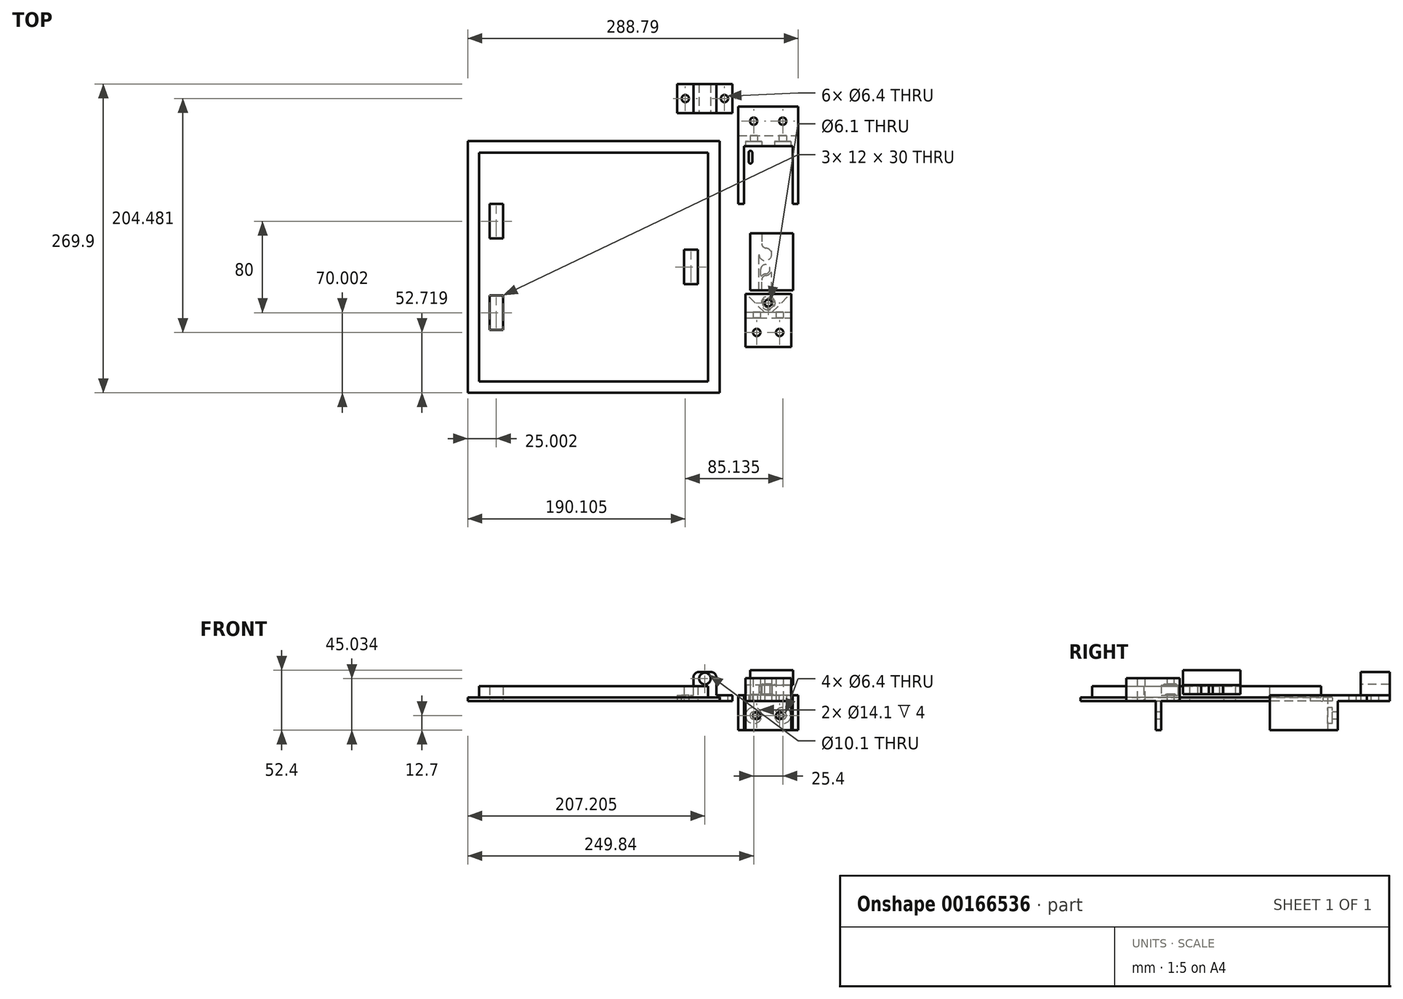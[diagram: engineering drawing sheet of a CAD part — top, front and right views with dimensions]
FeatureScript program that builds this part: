
annotation { "Feature Type Name" : "Feature", "Feature Type Description" : "" }
export const myFeature = defineFeature(function(context is Context, id is Id, definition is map)
    precondition{}
    {
        {
            var Q0;
            Q0=qCreatedBy(makeId("Top.planeOp"),FACE);
            var sketch = newSketch(context, id + "F0", { "sketchPlane" : qUnion([Q0])});
            skPoint(sketch, "E0.5", {"position": v(15.5, -15.5) * mm});
            skPoint(sketch, "E0.6", {"position": v(-15.5, -15.5) * mm});
            skPoint(sketch, "E0.7", {"position": v(-15.5, 15.5) * mm});
            skPoint(sketch, "E0.8", {"position": v(15.5, 15.5) * mm});
            skLineSegment(sketch, "E1.0", {"start": v(-21.25, 21.25) * mm, "end": v(-21.25, -21.25) * mm});
            skLineSegment(sketch, "E1.1", {"start": v(21.25, 21.25) * mm, "end": v(-21.25, 21.25) * mm});
            skLineSegment(sketch, "E1.2", {"start": v(21.25, 21.25) * mm, "end": v(21.25, -21.25) * mm});
            skLineSegment(sketch, "E1.3", {"start": v(21.25, -21.25) * mm, "end": v(-21.25, -21.25) * mm});
            skCircle(sketch, "E2.0", {"center": v(0, 0) * mm, "radius": 11.25 * mm});
            skCircle(sketch, "E3", {"center": v(-15.5, 15.5) * mm, "radius": 1.52 * mm});
            skCircle(sketch, "E4", {"center": v(15.5, 15.5) * mm, "radius": 1.52 * mm});
            skCircle(sketch, "E5", {"center": v(15.5, -15.5) * mm, "radius": 1.52 * mm});
            skCircle(sketch, "E6", {"center": v(-15.5, -15.5) * mm, "radius": 1.52 * mm});
            skLineSegment(sketch, "E7", {"start": v(-21.25, 21.25) * mm, "end": v(21.25, -21.25) * mm, "construction": true});
            skSolve(sketch);
        }
        {
            var Q0;
            Q0=qCreatedBy(makeId("Front.planeOp"),FACE);
            cPlane(context, id + "F1", {"entities" : qUnion([Q0]), "cplaneType" : CPlaneType.OFFSET, "offset" : 50 * mm, "oppositeDirection" : true, "width" : 150 * mm, "height" : 150 * mm});
        }
        {
            var Q0;
            Q0=qCreatedBy(id+"F1.planeOp",FACE);
            var sketch = newSketch(context, id + "F2", { "sketchPlane" : qUnion([Q0])});
            skLineSegment(sketch, "E8.bottom", {"start": v(-79.49, 5) * mm, "end": v(-65.39, 5) * mm});
            skLineSegment(sketch, "E8.top", {"start": v(-79.49, 0) * mm, "end": v(-31.19, 0) * mm});
            skLineSegment(sketch, "E8.left", {"start": v(-79.49, 5) * mm, "end": v(-79.49, 0) * mm});
            skLineSegment(sketch, "E8.right", {"start": v(-31.19, 5) * mm, "end": v(-31.19, 0) * mm});
            skCircle(sketch, "E9", {"center": v(-55.34, 19.63) * mm, "radius": 5.05 * mm});
            skLineSegment(sketch, "E10.bottom", {"start": v(-2.5, 24) * mm, "end": v(2.5, 24) * mm, "construction": true});
            skLineSegment(sketch, "E10.top", {"start": v(-2.5, 0) * mm, "end": v(2.5, 0) * mm, "construction": true});
            skLineSegment(sketch, "E10.left", {"start": v(-2.5, 24) * mm, "end": v(-2.5, 0) * mm, "construction": true});
            skLineSegment(sketch, "E10.right", {"start": v(2.5, 24) * mm, "end": v(2.5, 0) * mm, "construction": true});
            skLineSegment(sketch, "E11", {"start": v(-61.34, 27) * mm, "end": v(-49.34, 27) * mm, "construction": true});
            skCircle(sketch, "E12", {"center": v(-55.34, 19.63) * mm, "radius": 9.5 * mm, "construction": true});
            skPoint(sketch, "E13", {"position": v(-55.34, 5) * mm});
            skArc(sketch, "E14", {"start": v(-65.24, 21.36) * mm, "mid": v(-55.34, 9.58) * mm, "end": v(-45.43, 21.36) * mm});
            skLineSegment(sketch, "E15", {"start": v(-65.39, 5) * mm, "end": v(-65.39, 19.63) * mm});
            skLineSegment(sketch, "E16", {"start": v(-45.29, 5) * mm, "end": v(-45.29, 19.63) * mm});
            skLineSegment(sketch, "E17", {"start": v(-65.39, 5) * mm, "end": v(-45.29, 5) * mm});
            skLineSegment(sketch, "E18", {"start": v(-45.29, 5) * mm, "end": v(-31.19, 5) * mm});
            skLineSegment(sketch, "E19", {"start": v(-72.44, 6.24) * mm, "end": v(-72.44, -2.4) * mm, "construction": true});
            skPoint(sketch, "E19.startSnap0", {"position": v(-72.44, 5) * mm});
            skLineSegment(sketch, "E20", {"start": v(-38.24, 7.18) * mm, "end": v(-38.24, -1.8) * mm, "construction": true});
            skPoint(sketch, "E20.startSnap0", {"position": v(-38.24, 5) * mm});
            skPoint(sketch, "E21", {"position": v(0, 0) * mm});
            skLineSegment(sketch, "E22", {"start": v(-60.31, 25.5) * mm, "end": v(-50.36, 25.5) * mm});
            skPoint(sketch, "E23.visualSharp", {"position": v(-63.5, 25.5) * mm});
            skArc(sketch, "E23.filletArc", {"start": v(-60.31, 25.5) * mm, "mid": v(-63.53, 24.33) * mm, "end": v(-65.24, 21.36) * mm});
            skPoint(sketch, "E24.visualSharp", {"position": v(-47.17, 25.5) * mm});
            skArc(sketch, "E24.filletArc", {"start": v(-45.43, 21.36) * mm, "mid": v(-47.14, 24.33) * mm, "end": v(-50.36, 25.5) * mm});
            skLineSegment(sketch, "E25", {"start": v(-12.3, 2.5) * mm, "end": v(8.31, 2.5) * mm, "construction": true});
            skLineSegment(sketch, "E26.bottom", {"start": v(7, 5) * mm, "end": v(-7, 5) * mm, "construction": true});
            skLineSegment(sketch, "E26.top", {"start": v(7, 6) * mm, "end": v(-7, 6) * mm, "construction": true});
            skLineSegment(sketch, "E26.left", {"start": v(7, 5) * mm, "end": v(7, 6) * mm, "construction": true});
            skLineSegment(sketch, "E26.right", {"start": v(-7, 5) * mm, "end": v(-7, 6) * mm, "construction": true});
            skPoint(sketch, "E26.middle", {"position": v(0, 5.5) * mm});
            skPoint(sketch, "E26.middle.positionSnap0", {"position": v(0, 24) * mm});
            skPoint(sketch, "E26.centerSnap0", {"position": v(0, 24) * mm});
            skLineSegment(sketch, "E27.bottom", {"start": v(6.1, 6) * mm, "end": v(-6.1, 6) * mm, "construction": true});
            skLineSegment(sketch, "E27.top", {"start": v(6.1, 14) * mm, "end": v(-6.1, 14) * mm, "construction": true});
            skLineSegment(sketch, "E27.left", {"start": v(6.1, 6) * mm, "end": v(6.1, 14) * mm, "construction": true});
            skLineSegment(sketch, "E27.right", {"start": v(-6.1, 6) * mm, "end": v(-6.1, 14) * mm, "construction": true});
            skPoint(sketch, "E27.middle", {"position": v(0, 10) * mm});
            skLineSegment(sketch, "E28.bottom", {"start": v(-7, 14) * mm, "end": v(7, 14) * mm, "construction": true});
            skLineSegment(sketch, "E28.top", {"start": v(-7, 21.5) * mm, "end": v(7, 21.5) * mm, "construction": true});
            skLineSegment(sketch, "E28.left", {"start": v(-7, 14) * mm, "end": v(-7, 21.5) * mm, "construction": true});
            skLineSegment(sketch, "E28.right", {"start": v(7, 14) * mm, "end": v(7, 21.5) * mm, "construction": true});
            skPoint(sketch, "E28.middle", {"position": v(0, 17.75) * mm});
            skSolve(sketch);
        }
        {
            var Q0;
            Q0=makeQuery(id+"F2.imprint","IMPRINT",FACE,{"disambiguationData":[TD([[makeQuery(id+"F2.imprint","IMPRINT",EDGE,{"derivedFrom":sQuery(id+"F2.wireOp",EDGE,"E8.bottom")}),-1.0]])]});
            var Q1;
            {var subQ0=sQuery(id+"F2.wireOp",EDGE,"E15");Q1=makeQuery(id+"F2.imprint","IMPRINT",FACE,{"disambiguationData":[TD([[makeQuery(id+"F2.imprint","IMPRINT",EDGE,{"derivedFrom":subQ0}),-1.0]])]});}
            var Q2;
            Q2=makeQuery(id+"F2.imprint","IMPRINT",FACE,{"disambiguationData":[TD([[makeQuery(id+"F2.imprint","IMPRINT",EDGE,{"derivedFrom":sQuery(id+"F2.wireOp",EDGE,"E9")}),-1.0]])]});
            extrude(context, id + "F3", {"entities" : qUnion([Q0, Q1, Q2]), "oppositeDirection" : true, "depth" : 25.4 * mm});
        }
        {
            var Q0;
            Q0=makeQuery(id+"F3.opExtrude","SWEPT_FACE",FACE,{"disambiguationData":[OSD([sQuery(id+"F2.wireOp",EDGE,"E18")])]});
            var sketch = newSketch(context, id + "F4", { "sketchPlane" : qUnion([Q0])});
            skCircle(sketch, "E29", {"center": v(-38.24, 62.7) * mm, "radius": 3.2 * mm});
            skPoint(sketch, "E29.centerSnap0", {"position": v(-31.19, 62.7) * mm});
            skPoint(sketch, "E29.centerSnap1", {"position": v(-38.24, 50) * mm});
            skPoint(sketch, "E30.0", {"position": v(-72.44, 50) * mm});
            skCircle(sketch, "E31", {"center": v(-72.44, 62.7) * mm, "radius": 3.2 * mm});
            skSolve(sketch);
        }
        {
            var Q0;
            Q0=makeQuery(id+"F4.imprint","IMPRINT",FACE,{"disambiguationData":[TD([[makeQuery(id+"F4.imprint","IMPRINT",EDGE,{"derivedFrom":sQuery(id+"F4.wireOp",EDGE,"E31")}),1.0]])]});
            var Q1;
            Q1=makeQuery(id+"F4.imprint","IMPRINT",FACE,{"disambiguationData":[TD([[makeQuery(id+"F4.imprint","IMPRINT",EDGE,{"derivedFrom":sQuery(id+"F4.wireOp",EDGE,"E29")}),1.0]])]});
            extrude(context, id + "F5", {"entities" : qUnion([Q0, Q1]), "operationType" : NewBodyOperationType.REMOVE, "endBound" : BoundingType.UP_TO_NEXT, "oppositeDirection" : true, "depth" : 25 * mm});
        }
        {
            var Q0;
            Q0=qCreatedBy(makeId("Top.planeOp"),FACE);
            var sketch = newSketch(context, id + "F6", { "sketchPlane" : qUnion([Q0])});
            skPoint(sketch, "E32.0", {"position": v(-15.5, 15.5) * mm});
            skPoint(sketch, "E32.1", {"position": v(15.5, 15.5) * mm});
            skPoint(sketch, "E32.2", {"position": v(15.5, -15.5) * mm});
            skPoint(sketch, "E32.3", {"position": v(-15.5, -15.5) * mm});
            skPoint(sketch, "E32.4", {"position": v(0, 0) * mm});
            skLineSegment(sketch, "E33", {"start": v(-15.5, 15.5) * mm, "end": v(-15.5, 7.5) * mm});
            skLineSegment(sketch, "E34", {"start": v(15.5, 15.5) * mm, "end": v(15.5, 7.5) * mm});
            skLineSegment(sketch, "E35", {"start": v(0, 0) * mm, "end": v(0, -8) * mm});
            skLineSegment(sketch, "E36", {"start": v(-15.5, -15.5) * mm, "end": v(-15.5, -23.5) * mm});
            skLineSegment(sketch, "E37", {"start": v(15.5, -15.5) * mm, "end": v(15.5, -23.5) * mm});
            skArc(sketch, "E38.0.startCap", {"start": v(-17.05, 15.5) * mm, "mid": v(-15.5, 17.05) * mm, "end": v(-13.95, 15.5) * mm});
            skArc(sketch, "E38.0.endCap", {"start": v(-13.95, 7.5) * mm, "mid": v(-15.5, 5.95) * mm, "end": v(-17.05, 7.5) * mm});
            skLineSegment(sketch, "E38.0.left", {"start": v(-13.95, 15.5) * mm, "end": v(-13.95, 7.5) * mm});
            skLineSegment(sketch, "E38.0.right", {"start": v(-17.05, 15.5) * mm, "end": v(-17.05, 7.5) * mm});
            skArc(sketch, "E38.1.startCap", {"start": v(13.95, 15.5) * mm, "mid": v(15.5, 17.05) * mm, "end": v(17.05, 15.5) * mm});
            skArc(sketch, "E38.1.endCap", {"start": v(17.05, 7.5) * mm, "mid": v(15.5, 5.95) * mm, "end": v(13.95, 7.5) * mm});
            skLineSegment(sketch, "E38.1.left", {"start": v(17.05, 15.5) * mm, "end": v(17.05, 7.5) * mm});
            skLineSegment(sketch, "E38.1.right", {"start": v(13.95, 15.5) * mm, "end": v(13.95, 7.5) * mm});
            skArc(sketch, "E38.2.startCap", {"start": v(13.95, -15.5) * mm, "mid": v(15.5, -13.95) * mm, "end": v(17.05, -15.5) * mm});
            skArc(sketch, "E38.2.endCap", {"start": v(17.05, -23.5) * mm, "mid": v(15.5, -25.05) * mm, "end": v(13.95, -23.5) * mm});
            skLineSegment(sketch, "E38.2.left", {"start": v(17.05, -15.5) * mm, "end": v(17.05, -23.5) * mm});
            skLineSegment(sketch, "E38.2.right", {"start": v(13.95, -15.5) * mm, "end": v(13.95, -23.5) * mm});
            skArc(sketch, "E38.3.startCap", {"start": v(-17.05, -15.5) * mm, "mid": v(-15.5, -13.95) * mm, "end": v(-13.95, -15.5) * mm});
            skArc(sketch, "E38.3.endCap", {"start": v(-13.95, -23.5) * mm, "mid": v(-15.5, -25.05) * mm, "end": v(-17.05, -23.5) * mm});
            skLineSegment(sketch, "E38.3.left", {"start": v(-13.95, -15.5) * mm, "end": v(-13.95, -23.5) * mm});
            skLineSegment(sketch, "E38.3.right", {"start": v(-17.05, -15.5) * mm, "end": v(-17.05, -23.5) * mm});
            skArc(sketch, "E39.0.startCap", {"start": v(-11.25, 0) * mm, "mid": v(0, 11.25) * mm, "end": v(11.25, 0) * mm});
            skArc(sketch, "E39.0.endCap", {"start": v(11.25, -8) * mm, "mid": v(0, -19.25) * mm, "end": v(-11.25, -8) * mm});
            skLineSegment(sketch, "E39.0.left", {"start": v(11.25, 0) * mm, "end": v(11.25, -8) * mm});
            skLineSegment(sketch, "E39.0.right", {"start": v(-11.25, 0) * mm, "end": v(-11.25, -8) * mm});
            skLineSegment(sketch, "E40.0", {"start": v(21.25, 21.25) * mm, "end": v(-21.25, 21.25) * mm});
            skLineSegment(sketch, "E40.1", {"start": v(-21.25, 21.25) * mm, "end": v(-21.25, -29.25) * mm});
            skLineSegment(sketch, "E40.2", {"start": v(21.25, 21.25) * mm, "end": v(21.25, -29.25) * mm});
            skPoint(sketch, "E41.orphan", {"position": v(-21.25, -21.25) * mm});
            skPoint(sketch, "E42.orphan", {"position": v(21.25, -21.25) * mm});
            skLineSegment(sketch, "E43", {"start": v(-21.25, -29.25) * mm, "end": v(21.25, -29.25) * mm});
            skLineSegment(sketch, "E44", {"start": v(-21.25, -29.25) * mm, "end": v(-26.25, -29.25) * mm});
            skLineSegment(sketch, "E45", {"start": v(-26.25, -29.25) * mm, "end": v(-26.25, 30.25) * mm});
            skLineSegment(sketch, "E46", {"start": v(-26.25, 30.25) * mm, "end": v(26.25, 30.25) * mm});
            skLineSegment(sketch, "E47", {"start": v(26.25, 30.25) * mm, "end": v(26.25, -29.25) * mm});
            skLineSegment(sketch, "E48", {"start": v(26.25, -29.25) * mm, "end": v(21.25, -29.25) * mm});
            skLineSegment(sketch, "E49", {"start": v(26.25, 30.25) * mm, "end": v(26.25, 55.65) * mm});
            skLineSegment(sketch, "E50", {"start": v(26.25, 55.65) * mm, "end": v(-26.25, 55.65) * mm});
            skLineSegment(sketch, "E51", {"start": v(-26.25, 55.65) * mm, "end": v(-26.25, 30.25) * mm});
            skCircle(sketch, "E52", {"center": v(-12.7, 42.95) * mm, "radius": 3.2 * mm});
            skPoint(sketch, "E52.centerSnap0", {"position": v(-26.25, 42.95) * mm});
            skCircle(sketch, "E53", {"center": v(12.7, 42.95) * mm, "radius": 3.2 * mm});
            skPoint(sketch, "E53.centerSnap0", {"position": v(26.25, 42.95) * mm});
            skPoint(sketch, "E54", {"position": v(0, 42.95) * mm});
            skSolve(sketch);
        }
        {
            var Q0;
            Q0=makeQuery(id+"F6.imprint","IMPRINT",FACE,{"disambiguationData":[TD([[makeQuery(id+"F6.imprint","IMPRINT",EDGE,{"derivedFrom":sQuery(id+"F6.wireOp",EDGE,"E38.0.startCap")}),1.0]])]});
            var Q1;
            Q1=makeQuery(id+"F6.imprint","IMPRINT",FACE,{"disambiguationData":[TD([[makeQuery(id+"F6.imprint","IMPRINT",EDGE,{"derivedFrom":sQuery(id+"F6.wireOp",EDGE,"E40.0")}),-1.0]])]});
            var Q2;
            Q2=makeQuery(id+"F6.imprint","IMPRINT",FACE,{"disambiguationData":[TD([[makeQuery(id+"F6.imprint","IMPRINT",EDGE,{"derivedFrom":sQuery(id+"F6.wireOp",EDGE,"E46")}),1.0]])]});
            extrude(context, id + "F7", {"entities" : qUnion([Q0, Q1, Q2]), "depth" : 5 * mm});
        }
        {
            var Q0;
            Q0=makeQuery(id+"F6.imprint","IMPRINT",FACE,{"disambiguationData":[TD([[makeQuery(id+"F6.imprint","IMPRINT",EDGE,{"derivedFrom":sQuery(id+"F6.wireOp",EDGE,"E40.0")}),-1.0]])]});
            extrude(context, id + "F8", {"entities" : qUnion([Q0]), "operationType" : NewBodyOperationType.ADD, "oppositeDirection" : true, "depth" : 25.4 * mm});
        }
        {
            var Q0;
            Q0=makeQuery(id+"F8.opExtrude","SWEPT_FACE",FACE,{"disambiguationData":[OSD([sQuery(id+"F6.wireOp",EDGE,"E40.0")])]});
            var sketch = newSketch(context, id + "F9", { "sketchPlane" : qUnion([Q0])});
            skPoint(sketch, "E55.0", {"position": v(12.7, 0) * mm});
            skPoint(sketch, "E55.1", {"position": v(-12.7, 0) * mm});
            skCircle(sketch, "E56", {"center": v(12.7, -12.7) * mm, "radius": 3.2 * mm});
            skPoint(sketch, "E56.centerSnap0", {"position": v(21.25, -12.7) * mm});
            skCircle(sketch, "E57", {"center": v(-12.7, -12.7) * mm, "radius": 3.2 * mm});
            skCircle(sketch, "E58", {"center": v(-12.7, -12.7) * mm, "radius": 7.05 * mm});
            skCircle(sketch, "E59", {"center": v(12.7, -12.7) * mm, "radius": 7.05 * mm});
            skSolve(sketch);
        }
        {
            var Q0;
            Q0=makeQuery(id+"F9.imprint","IMPRINT",FACE,{"disambiguationData":[TD([[makeQuery(id+"F9.imprint","IMPRINT",EDGE,{"derivedFrom":sQuery(id+"F9.wireOp",EDGE,"E57")}),1.0]])]});
            var Q1;
            Q1=makeQuery(id+"F9.imprint","IMPRINT",FACE,{"disambiguationData":[TD([[makeQuery(id+"F9.imprint","IMPRINT",EDGE,{"derivedFrom":sQuery(id+"F9.wireOp",EDGE,"E56")}),1.0]])]});
            extrude(context, id + "F10", {"entities" : qUnion([Q0, Q1]), "operationType" : NewBodyOperationType.REMOVE, "endBound" : BoundingType.UP_TO_NEXT, "oppositeDirection" : true, "depth" : 25 * mm});
        }
        {
            var Q0;
            Q0=makeQuery(id+"F9.imprint","IMPRINT",FACE,{"disambiguationData":[TD([[makeQuery(id+"F9.imprint","IMPRINT",EDGE,{"derivedFrom":sQuery(id+"F9.wireOp",EDGE,"E57")}),-1.0]])]});
            var Q1;
            Q1=makeQuery(id+"F9.imprint","IMPRINT",FACE,{"disambiguationData":[TD([[makeQuery(id+"F9.imprint","IMPRINT",EDGE,{"derivedFrom":sQuery(id+"F9.wireOp",EDGE,"E56")}),-1.0]])]});
            extrude(context, id + "F11", {"entities" : qUnion([Q0, Q1]), "operationType" : NewBodyOperationType.REMOVE, "oppositeDirection" : true, "depth" : 4 * mm});
        }
        {
            var Q0;
            Q0=qCreatedBy(makeId("Top.planeOp"),FACE);
            var sketch = newSketch(context, id + "F12", { "sketchPlane" : qUnion([Q0])});
            skLineSegment(sketch, "E60.bottom", {"start": v(-20, -124.08) * mm, "end": v(20, -124.08) * mm});
            skLineSegment(sketch, "E60.top", {"start": v(-20, -129.08) * mm, "end": v(20, -129.08) * mm});
            skLineSegment(sketch, "E60.left", {"start": v(-20, -124.08) * mm, "end": v(-20, -129.08) * mm});
            skLineSegment(sketch, "E60.right", {"start": v(20, -124.08) * mm, "end": v(20, -129.08) * mm});
            skCircle(sketch, "E61", {"center": v(0, -116.08) * mm, "radius": 3.05 * mm});
            skCircle(sketch, "E62", {"center": v(-10, -141.78) * mm, "radius": 3.2 * mm});
            skCircle(sketch, "E63.cCircle", {"center": v(0, -116.08) * mm, "radius": 5 * mm, "construction": true});
            skLineSegment(sketch, "E63.0", {"start": v(5, -113.2) * mm, "end": v(5, -118.97) * mm});
            skLineSegment(sketch, "E63.1", {"start": v(5, -118.97) * mm, "end": v(0, -121.85) * mm});
            skLineSegment(sketch, "E63.2", {"start": v(0, -121.85) * mm, "end": v(-5, -118.97) * mm});
            skLineSegment(sketch, "E63.3", {"start": v(-5, -118.97) * mm, "end": v(-5, -113.2) * mm});
            skLineSegment(sketch, "E63.4", {"start": v(-5, -113.2) * mm, "end": v(0, -110.3) * mm});
            skLineSegment(sketch, "E63.5", {"start": v(0, -110.3) * mm, "end": v(5, -113.2) * mm});
            skPoint(sketch, "E63.0.midPoint", {"position": v(5, -116.08) * mm});
            skPoint(sketch, "E64", {"position": v(0, -124.08) * mm});
            skLineSegment(sketch, "E65.bottom", {"start": v(20, -124.08) * mm, "end": v(-20, -124.08) * mm});
            skLineSegment(sketch, "E65.top", {"start": v(20, -108.08) * mm, "end": v(-20, -108.08) * mm});
            skLineSegment(sketch, "E65.left", {"start": v(20, -124.08) * mm, "end": v(20, -108.08) * mm});
            skLineSegment(sketch, "E65.right", {"start": v(-20, -124.08) * mm, "end": v(-20, -108.08) * mm});
            skLineSegment(sketch, "E66.top", {"start": v(-20, -154.48) * mm, "end": v(20, -154.48) * mm});
            skLineSegment(sketch, "E66.left", {"start": v(-20, -129.08) * mm, "end": v(-20, -154.48) * mm});
            skLineSegment(sketch, "E66.right", {"start": v(20, -129.08) * mm, "end": v(20, -154.48) * mm});
            skPoint(sketch, "E66.middle", {"position": v(0, -141.78) * mm});
            skCircle(sketch, "E67", {"center": v(0, -116.08) * mm, "radius": 8 * mm, "construction": true});
            skLineSegment(sketch, "E68", {"start": v(-3.31, -124.08) * mm, "end": v(-20, -107.4) * mm});
            skLineSegment(sketch, "E69", {"start": v(3.31, -124.08) * mm, "end": v(20, -107.4) * mm});
            skCircle(sketch, "E70", {"center": v(10, -141.78) * mm, "radius": 3.2 * mm});
            skSolve(sketch);
        }
        {
            var Q0;
            Q0=makeQuery(id+"F12.imprint","IMPRINT",FACE,{"disambiguationData":[TD([[makeQuery(id+"F12.imprint","IMPRINT",EDGE,{"derivedFrom":sQuery(id+"F12.wireOp",EDGE,"E60.left")}),1.0]])]});
            var Q1;
            Q1=makeQuery(id+"F12.imprint","IMPRINT",FACE,{"disambiguationData":[TD([[makeQuery(id+"F12.imprint","IMPRINT",EDGE,{"derivedFrom":sQuery(id+"F12.wireOp",EDGE,"E62")}),-1.0]])]});
            var Q2;
            {var subQ1=sQuery(id+"F12.wireOp",EDGE,"E65.bottom");var subQ3=sQuery(id+"F12.wireOp",EDGE,"E68");var subQ4=makeQuery(id+"F12.imprint","INTERSECT",VERTEX,{"derivedFrom":[subQ1,subQ3]});Q2=makeQuery(id+"F12.imprint","IMPRINT",FACE,{"disambiguationData":[TD([[makeQuery(id+"F12.imprint","IMPRINT",EDGE,{"disambiguationData":[TD([[subQ4,-1.0]])],"derivedFrom":subQ3}),1.0]])]});}
            var Q3;
            {var subQ1=sQuery(id+"F12.wireOp",EDGE,"E65.bottom");var subQ3=sQuery(id+"F12.wireOp",EDGE,"E69");var subQ4=makeQuery(id+"F12.imprint","INTERSECT",VERTEX,{"derivedFrom":[subQ1,subQ3]});Q3=makeQuery(id+"F12.imprint","IMPRINT",FACE,{"disambiguationData":[TD([[makeQuery(id+"F12.imprint","IMPRINT",EDGE,{"disambiguationData":[TD([[subQ4,-1.0]])],"derivedFrom":subQ3}),-1.0]])]});}
            extrude(context, id + "F13", {"entities" : qUnion([Q0, Q1, Q2, Q3]), "depth" : (10 + 5) * mm});
        }
        {
            var Q0;
            Q0=makeQuery(id+"F12.imprint","IMPRINT",FACE,{"disambiguationData":[TD([[makeQuery(id+"F12.imprint","IMPRINT",EDGE,{"derivedFrom":sQuery(id+"F12.wireOp",EDGE,"E63.0")}),1.0]])]});
            var Q1;
            Q1=makeQuery(id+"F12.imprint","IMPRINT",FACE,{"disambiguationData":[TD([[makeQuery(id+"F12.imprint","IMPRINT",EDGE,{"derivedFrom":sQuery(id+"F12.wireOp",EDGE,"E61")}),-1.0]])]});
            extrude(context, id + "F14", {"entities" : qUnion([Q0, Q1]), "operationType" : NewBodyOperationType.ADD, "depth" : 5 * mm});
        }
        {
            var Q0;
            Q0=makeQuery(id+"F13.opExtrude","CAP_FACE",FACE,{"disambiguationData":[OSD([sQuery(id+"F12.wireOp",EDGE,"E60.left"),sQuery(id+"F12.wireOp",EDGE,"E60.right"),sQuery(id+"F12.wireOp",EDGE,"E65.bottom"),sQuery(id+"F12.wireOp",EDGE,"E60.top")])],"isStart":false});
            var sketch = newSketch(context, id + "F15", { "sketchPlane" : qUnion([Q0])});
            skLineSegment(sketch, "E71.1", {"start": v(-20, -154.48) * mm, "end": v(20, -154.48) * mm});
            skCircle(sketch, "E72.0", {"center": v(-10, -141.78) * mm, "radius": 3.2 * mm});
            skLineSegment(sketch, "E73.0", {"start": v(20, -108.08) * mm, "end": v(20, -154.48) * mm});
            skCircle(sketch, "E73.1", {"center": v(10, -141.78) * mm, "radius": 3.2 * mm});
            skLineSegment(sketch, "E73.2", {"start": v(20, -108.08) * mm, "end": v(19.31, -108.08) * mm});
            skLineSegment(sketch, "E74.2", {"start": v(-19.31, -108.08) * mm, "end": v(-20, -108.08) * mm});
            skLineSegment(sketch, "E74.3", {"start": v(-20, -108.08) * mm, "end": v(-20, -154.48) * mm});
            skLineSegment(sketch, "E75.0", {"start": v(19.31, -108.08) * mm, "end": v(-19.31, -108.08) * mm});
            skCircle(sketch, "E76.0", {"center": v(0, -116.08) * mm, "radius": 3.05 * mm});
            skSolve(sketch);
        }
        {
            var Q0;
            Q0=makeQuery(id+"F15.imprint","IMPRINT",FACE,{"disambiguationData":[TD([[makeQuery(id+"F15.imprint","IMPRINT",EDGE,{"derivedFrom":sQuery(id+"F15.wireOp",EDGE,"E71.1")}),1.0]])]});
            var Q1;
            Q1=makeQuery(id+"F15.imprint","IMPRINT",FACE,{"disambiguationData":[TD([[makeQuery(id+"F15.imprint","IMPRINT",EDGE,{"derivedFrom":sQuery(id+"F15.wireOp",EDGE,"E75.0")}),1.0]])]});
            extrude(context, id + "F16", {"entities" : qUnion([Q0, Q1]), "operationType" : NewBodyOperationType.ADD, "depth" : 5 * mm});
        }
        {
            var Q0;
            Q0=makeQuery(id+"F12.imprint","IMPRINT",FACE,{"disambiguationData":[TD([[makeQuery(id+"F12.imprint","IMPRINT",EDGE,{"derivedFrom":sQuery(id+"F12.wireOp",EDGE,"E60.left")}),1.0]])]});
            extrude(context, id + "F17", {"entities" : qUnion([Q0]), "operationType" : NewBodyOperationType.ADD, "oppositeDirection" : true, "depth" : 25.4 * mm});
        }
        {
            var Q0;
            Q0=makeQuery(id+"F17.opExtrude","SWEPT_FACE",FACE,{"disambiguationData":[OSD([sQuery(id+"F12.wireOp",EDGE,"E60.top")])]});
            var sketch = newSketch(context, id + "F18", { "sketchPlane" : qUnion([Q0])});
            skCircle(sketch, "E77", {"center": v(-10, -12.7) * mm, "radius": 3.2 * mm});
            skPoint(sketch, "E77.centerSnap0", {"position": v(-20, -12.7) * mm});
            skPoint(sketch, "E78.0", {"position": v(10, 0) * mm});
            skPoint(sketch, "E78.1", {"position": v(-10, 0) * mm});
            skCircle(sketch, "E79", {"center": v(10, -12.7) * mm, "radius": 3.2 * mm});
            skSolve(sketch);
        }
        {
            var Q0;
            Q0=makeQuery(id+"F18.imprint","IMPRINT",FACE,{"disambiguationData":[TD([[makeQuery(id+"F18.imprint","IMPRINT",EDGE,{"derivedFrom":sQuery(id+"F18.wireOp",EDGE,"E77")}),1.0]])]});
            var Q1;
            Q1=makeQuery(id+"F18.imprint","IMPRINT",FACE,{"disambiguationData":[TD([[makeQuery(id+"F18.imprint","IMPRINT",EDGE,{"derivedFrom":sQuery(id+"F18.wireOp",EDGE,"E79")}),1.0]])]});
            extrude(context, id + "F19", {"entities" : qUnion([Q0, Q1]), "operationType" : NewBodyOperationType.REMOVE, "endBound" : BoundingType.UP_TO_NEXT, "oppositeDirection" : true, "depth" : 25 * mm});
        }
        {
            var Q0;
            Q0=makeQuery(id+"F14.opExtrude","CAP_FACE",FACE,{"disambiguationData":[OSD([sQuery(id+"F12.wireOp",EDGE,"E61"),sQuery(id+"F12.wireOp",EDGE,"E65.bottom"),sQuery(id+"F12.wireOp",EDGE,"E65.top"),sQuery(id+"F12.wireOp",EDGE,"E65.left"),sQuery(id+"F12.wireOp",EDGE,"E65.right"),sQuery(id+"F12.wireOp",EDGE,"E68"),sQuery(id+"F12.wireOp",EDGE,"E69")])],"isStart":false});
            var sketch = newSketch(context, id + "F20", { "sketchPlane" : qUnion([Q0])});
            skCircle(sketch, "E80.0", {"center": v(0, -116.08) * mm, "radius": 3.05 * mm});
            skCircle(sketch, "E81", {"center": v(0, -116.08) * mm, "radius": 5.05 * mm});
            skSolve(sketch);
        }
        {
            var Q0;
            Q0=makeQuery(id+"F16.opExtrude","CAP_FACE",FACE,{"disambiguationData":[OSD([sQuery(id+"F15.wireOp",EDGE,"ec6f7756-acda-49ed-b834-6cc59ef4dbf2.4"),sQuery(id+"F15.wireOp",EDGE,"a8c349f3-6dde-49f4-9578-254d6a36f4ff.0"),sQuery(id+"F15.wireOp",EDGE,"E71.0"),sQuery(id+"F15.wireOp",EDGE,"E71.1"),sQuery(id+"F15.wireOp",EDGE,"E71.2"),sQuery(id+"F15.wireOp",EDGE,"b8334c2e-c150-45c0-b4fa-ddddea4c770d.0"),sQuery(id+"F15.wireOp",EDGE,"b8334c2e-c150-45c0-b4fa-ddddea4c770d.1"),sQuery(id+"F15.wireOp",EDGE,"E72.0")])],"isStart":true});
            var sketch = newSketch(context, id + "F21", { "sketchPlane" : qUnion([Q0])});
            skCircle(sketch, "E82.0", {"center": v(0, 116.08) * mm, "radius": 5.05 * mm});
            skCircle(sketch, "E83.0", {"center": v(0, 116.08) * mm, "radius": 3.05 * mm});
            skSolve(sketch);
        }
        {
            var Q0;
            Q0=makeQuery(id+"F20.imprint","IMPRINT",FACE,{"disambiguationData":[TD([[makeQuery(id+"F20.imprint","IMPRINT",EDGE,{"derivedFrom":sQuery(id+"F20.wireOp",EDGE,"E80.0")}),-1.0]])]});
            extrude(context, id + "F22", {"entities" : qUnion([Q0]), "operationType" : NewBodyOperationType.ADD, "depth" : 1 * mm});
        }
        {
            var Q0;
            Q0=makeQuery(id+"F21.imprint","IMPRINT",FACE,{"disambiguationData":[TD([[makeQuery(id+"F21.imprint","IMPRINT",EDGE,{"derivedFrom":sQuery(id+"F21.wireOp",EDGE,"E82.0")}),-1.0]])]});
            extrude(context, id + "F23", {"entities" : qUnion([Q0]), "operationType" : NewBodyOperationType.ADD, "depth" : 1 * mm});
        }
        {
            var Q0;
            Q0=makeQuery(id+"F22.opExtrude","CAP_EDGE",EDGE,{"disambiguationData":[OSD([sQuery(id+"F20.wireOp",EDGE,"E81")])],"isStart":false});
            var Q1;
            Q1=makeQuery(id+"F23.opExtrude","CAP_EDGE",EDGE,{"disambiguationData":[OSD([sQuery(id+"F21.wireOp",EDGE,"E82.0")])],"isStart":false});
            chamfer(context, id + "F24", {"entities" : qUnion([Q0, Q1]), "width" : 1 * mm, "tangentPropagation" : true});
        }
        {
            var Q0;
            Q0=qCreatedBy(makeId("Front.planeOp"),FACE);
            cPlane(context, id + "F25", {"entities" : qUnion([Q0]), "cplaneType" : CPlaneType.OFFSET, "offset" : 80 * mm, "width" : 150 * mm, "height" : 150 * mm});
        }
        {
            var Q0;
            Q0=qCreatedBy(id+"F25.planeOp",FACE);
            var sketch = newSketch(context, id + "F26", { "sketchPlane" : qUnion([Q0])});
            skLineSegment(sketch, "E84.0", {"start": v(-61.34, 27) * mm, "end": v(-49.34, 27) * mm, "construction": true});
            skPoint(sketch, "E85.0", {"position": v(0, 10) * mm});
            skLineSegment(sketch, "E86.bottom", {"start": v(-15.75, 27) * mm, "end": v(21.76, 27) * mm});
            skLineSegment(sketch, "E86.top", {"start": v(-15.75, 14) * mm, "end": v(21.76, 14) * mm});
            skLineSegment(sketch, "E86.left", {"start": v(-15.75, 27) * mm, "end": v(-15.75, 14) * mm});
            skLineSegment(sketch, "E86.right", {"start": v(21.76, 27) * mm, "end": v(21.76, 14) * mm});
            skLineSegment(sketch, "E87", {"start": v(-15.75, 14) * mm, "end": v(-15.75, 6) * mm});
            skLineSegment(sketch, "E88", {"start": v(-15.75, 6) * mm, "end": v(3, 6) * mm});
            skLineSegment(sketch, "E89", {"start": v(3, 6) * mm, "end": v(3, 14) * mm});
            skPoint(sketch, "E90", {"position": v(3, 10) * mm});
            skSolve(sketch);
        }
        {
            var Q0;
            Q0=makeQuery(id+"F26.imprint","IMPRINT",FACE,{"disambiguationData":[TD([[makeQuery(id+"F26.imprint","IMPRINT",EDGE,{"derivedFrom":sQuery(id+"F26.wireOp",EDGE,"E86.bottom")}),-1.0]])]});
            var Q1;
            {var subQ0=sQuery(id+"F26.wireOp",EDGE,"E87");Q1=makeQuery(id+"F26.imprint","IMPRINT",FACE,{"disambiguationData":[TD([[makeQuery(id+"F26.imprint","IMPRINT",EDGE,{"derivedFrom":subQ0}),1.0]])]});}
            extrude(context, id + "F27", {"entities" : qUnion([Q0, Q1]), "endBound" : BoundingType.SYMMETRIC, "depth" : 50 * mm});
        }
        {
            var Q0;
            Q0=makeQuery(id+"F27.opExtrude","SWEPT_FACE",FACE,{"disambiguationData":[OSD([sQuery(id+"F26.wireOp",EDGE,"E88")])]});
            var sketch = newSketch(context, id + "F28", { "sketchPlane" : qUnion([Q0])});
            skPoint(sketch, "E91.0", {"position": v(0, 0) * mm});
            skLineSegment(sketch, "E92", {"start": v(0, 55) * mm, "end": v(0, 105) * mm, "construction": true});
            skCircle(sketch, "E93", {"center": v(0, 80) * mm, "radius": 6.5 * mm, "construction": true});
            skLineSegment(sketch, "E94", {"start": v(-8, 105) * mm, "end": v(-8, 55) * mm});
            skLineSegment(sketch, "E95", {"start": v(-6.5, 91.88) * mm, "end": v(-6.5, 86.5) * mm});
            skLineSegment(sketch, "E96", {"start": v(-5.6, 105) * mm, "end": v(-5.6, 95.96) * mm});
            skArc(sketch, "E97", {"start": v(-6.5, 86.5) * mm, "mid": v(0.2, 83.54) * mm, "end": v(-2.12, 90.48) * mm});
            skArc(sketch, "E98", {"start": v(-5.63, 92.22) * mm, "mid": v(-4.04, 91.03) * mm, "end": v(-2.12, 90.48) * mm});
            skArc(sketch, "E99", {"start": v(-5.63, 92.22) * mm, "mid": v(-6.18, 92.34) * mm, "end": v(-6.5, 91.88) * mm});
            skArc(sketch, "E100", {"start": v(-5.6, 95.96) * mm, "mid": v(-4.56, 93.27) * mm, "end": v(-1.98, 91.98) * mm});
            skArc(sketch, "E101.trimOffspring", {"start": v(-8, 86.5) * mm, "mid": v(-2.5, 81) * mm, "end": v(3, 86.5) * mm});
            skLineSegment(sketch, "E102.0", {"start": v(3, 105) * mm, "end": v(3, 55) * mm});
            skArc(sketch, "E103", {"start": v(2.08, 89.54) * mm, "mid": v(2.64, 89.34) * mm, "end": v(3, 89.82) * mm});
            skArc(sketch, "E104.trimOffspring", {"start": v(2.08, 89.54) * mm, "mid": v(0.33, 91.22) * mm, "end": v(-1.98, 91.98) * mm});
            skArc(sketch, "E105.MirrorCS", {"start": v(-5.6, 64.04) * mm, "mid": v(-4.56, 66.73) * mm, "end": v(-1.98, 68.02) * mm});
            skArc(sketch, "E106.MirrorCS", {"start": v(2.08, 70.46) * mm, "mid": v(0.33, 68.78) * mm, "end": v(-1.98, 68.02) * mm});
            skArc(sketch, "E107.MirrorCS", {"start": v(2.08, 70.46) * mm, "mid": v(2.64, 70.66) * mm, "end": v(3, 70.18) * mm});
            skArc(sketch, "E108.MirrorCS", {"start": v(-6.5, 73.5) * mm, "mid": v(0.2, 76.46) * mm, "end": v(-2.12, 69.52) * mm});
            skArc(sketch, "E109.MirrorCS", {"start": v(-5.63, 67.78) * mm, "mid": v(-4.04, 68.97) * mm, "end": v(-2.12, 69.52) * mm});
            skArc(sketch, "E110.MirrorCS", {"start": v(-5.63, 67.78) * mm, "mid": v(-6.18, 67.66) * mm, "end": v(-6.5, 68.12) * mm});
            skLineSegment(sketch, "E111.MirrorCS", {"start": v(-6.5, 68.12) * mm, "end": v(-6.5, 73.5) * mm});
            skArc(sketch, "E112.MirrorCS", {"start": v(-8, 73.5) * mm, "mid": v(-2.5, 79) * mm, "end": v(3, 73.5) * mm});
            skLineSegment(sketch, "E113.MirrorCS", {"start": v(-5.6, 55) * mm, "end": v(-5.6, 64.04) * mm});
            skSolve(sketch);
        }
        {
            var Q0;
            Q0=makeQuery(id+"F28.imprint","IMPRINT",FACE,{"disambiguationData":[TD([[makeQuery(id+"F28.imprint","IMPRINT",EDGE,{"derivedFrom":sQuery(id+"F28.wireOp",EDGE,"E95")}),-1.0]])]});
            var Q1;
            Q1=makeQuery(id+"F28.imprint","IMPRINT",FACE,{"disambiguationData":[TD([[makeQuery(id+"F28.imprint","IMPRINT",EDGE,{"derivedFrom":sQuery(id+"F28.wireOp",EDGE,"25bd4ca6-cc25-4745-a894-4c1708b292110.MirrorCS")}),1.0]])]});
            var Q2;
            {var subQ0=sQuery(id+"F28.wireOp",EDGE,"E101.trimOffspring");Q2=makeQuery(id+"F28.imprint","IMPRINT",FACE,{"disambiguationData":[TD([[makeQuery(id+"F28.imprint","IMPRINT",EDGE,{"derivedFrom":subQ0}),-1.0]])]});}
            var Q3;
            Q3=makeQuery(id+"F28.imprint","IMPRINT",FACE,{"disambiguationData":[TD([[makeQuery(id+"F28.imprint","IMPRINT",EDGE,{"derivedFrom":sQuery(id+"F28.wireOp",EDGE,"E105.MirrorCS")}),1.0]])]});
            var Q4;
            Q4=makeQuery(id+"F27.opExtrude","SWEPT_FACE",FACE,{"disambiguationData":[OSD([sQuery(id+"F26.wireOp",EDGE,"E86.top")])]});
            extrude(context, id + "F29", {"entities" : qUnion([Q0, Q1, Q2, Q3]), "operationType" : NewBodyOperationType.REMOVE, "endBound" : BoundingType.UP_TO_SURFACE, "oppositeDirection" : true, "endBoundEntityFace" : qUnion([Q4]), "depth" : 25 * mm});
        }
        {
            var Q0;
            Q0=qCreatedBy(makeId("Top.planeOp"),FACE);
            var sketch = newSketch(context, id + "F30", { "sketchPlane" : qUnion([Q0])});
            skLineSegment(sketch, "E114.bottom", {"start": v(-262.54, 25.5) * mm, "end": v(-42.54, 25.5) * mm});
            skLineSegment(sketch, "E114.top", {"start": v(-262.54, -194.5) * mm, "end": v(-42.54, -194.5) * mm});
            skLineSegment(sketch, "E114.left", {"start": v(-262.54, 25.5) * mm, "end": v(-262.54, -194.5) * mm});
            skLineSegment(sketch, "E114.right", {"start": v(-42.54, 25.5) * mm, "end": v(-42.54, -194.5) * mm});
            skLineSegment(sketch, "E115.bottom", {"start": v(-243.54, -29.5) * mm, "end": v(-231.54, -29.5) * mm});
            skLineSegment(sketch, "E115.top", {"start": v(-243.54, -59.5) * mm, "end": v(-231.54, -59.5) * mm});
            skLineSegment(sketch, "E115.left", {"start": v(-243.54, -29.5) * mm, "end": v(-243.54, -59.5) * mm});
            skLineSegment(sketch, "E115.right", {"start": v(-231.54, -29.5) * mm, "end": v(-231.54, -59.5) * mm});
            skLineSegment(sketch, "E116", {"start": v(-262.54, -84.5) * mm, "end": v(-42.54, -84.5) * mm, "construction": true});
            skLineSegment(sketch, "E117", {"start": v(-152.54, 25.5) * mm, "end": v(-152.54, -194.5) * mm, "construction": true});
            skLineSegment(sketch, "E118.MirrorCS", {"start": v(-243.54, -109.5) * mm, "end": v(-231.54, -109.5) * mm});
            skLineSegment(sketch, "E119.MirrorCS", {"start": v(-231.54, -139.5) * mm, "end": v(-231.54, -109.5) * mm});
            skLineSegment(sketch, "E120.MirrorCS", {"start": v(-243.54, -139.5) * mm, "end": v(-243.54, -109.5) * mm});
            skLineSegment(sketch, "E121.MirrorCS", {"start": v(-243.54, -139.5) * mm, "end": v(-231.54, -139.5) * mm});
            skLineSegment(sketch, "E122.bottom", {"start": v(-73.54, -69.5) * mm, "end": v(-61.54, -69.5) * mm});
            skLineSegment(sketch, "E122.top", {"start": v(-73.54, -99.5) * mm, "end": v(-61.54, -99.5) * mm});
            skLineSegment(sketch, "E122.left", {"start": v(-73.54, -69.5) * mm, "end": v(-73.54, -99.5) * mm});
            skLineSegment(sketch, "E122.right", {"start": v(-61.54, -69.5) * mm, "end": v(-61.54, -99.5) * mm});
            skPoint(sketch, "E123", {"position": v(-73.54, -84.5) * mm});
            skLineSegment(sketch, "E124", {"start": v(-237.54, -5.56) * mm, "end": v(-237.54, -84.5) * mm, "construction": true});
            skPoint(sketch, "E124.startSnap0", {"position": v(-237.54, -29.5) * mm});
            skLineSegment(sketch, "E125", {"start": v(-67.54, -64.04) * mm, "end": v(-67.54, -108.13) * mm, "construction": true});
            skPoint(sketch, "E125.startSnap0", {"position": v(-67.54, -69.5) * mm});
            skPoint(sketch, "E126", {"position": v(-67.54, -84.5) * mm});
            skPoint(sketch, "E127", {"position": v(-152.54, -84.5) * mm});
            skSolve(sketch);
        }
        {
            var Q0;
            Q0=makeQuery(id+"F30.imprint","IMPRINT",FACE,{"disambiguationData":[TD([[makeQuery(id+"F30.imprint","IMPRINT",EDGE,{"derivedFrom":sQuery(id+"F30.wireOp",EDGE,"E114.bottom")}),-1.0]])]});
            extrude(context, id + "F31", {"entities" : qUnion([Q0]), "depth" : 3 * mm});
        }
        {
            var Q0;
            Q0=makeQuery(id+"F31.opExtrude","CAP_EDGE",EDGE,{"disambiguationData":[OSD([sQuery(id+"F30.wireOp",EDGE,"E115.bottom")])],"isStart":true});
            var Q1;
            Q1=makeQuery(id+"F31.opExtrude","CAP_FACE",FACE,{"disambiguationData":[OSD([sQuery(id+"F30.wireOp",EDGE,"E114.bottom"),sQuery(id+"F30.wireOp",EDGE,"E114.top"),sQuery(id+"F30.wireOp",EDGE,"E114.left"),sQuery(id+"F30.wireOp",EDGE,"E114.right"),sQuery(id+"F30.wireOp",EDGE,"E115.bottom"),sQuery(id+"F30.wireOp",EDGE,"E115.top"),sQuery(id+"F30.wireOp",EDGE,"E115.left"),sQuery(id+"F30.wireOp",EDGE,"E115.right"),sQuery(id+"F30.wireOp",EDGE,"E118.MirrorCS"),sQuery(id+"F30.wireOp",EDGE,"E119.MirrorCS"),sQuery(id+"F30.wireOp",EDGE,"E120.MirrorCS"),sQuery(id+"F30.wireOp",EDGE,"E121.MirrorCS"),sQuery(id+"F30.wireOp",EDGE,"E122.bottom"),sQuery(id+"F30.wireOp",EDGE,"E122.top"),sQuery(id+"F30.wireOp",EDGE,"E122.left"),sQuery(id+"F30.wireOp",EDGE,"E122.right")])],"isStart":true});
            cPlane(context, id + "F32", {"entities" : qUnion([Q0, Q1]), "cplaneType" : CPlaneType.LINE_ANGLE, "offset" : 25 * mm, "angle" : 90 * degree, "width" : 150 * mm, "height" : 150 * mm});
        }
        {
            var Q0;
            Q0=qCreatedBy(id+"F32.planeOp",FACE);
            var sketch = newSketch(context, id + "F33", { "sketchPlane" : qUnion([Q0])});
            skPoint(sketch, "E128.0", {"position": v(-231.54, 0) * mm});
            skPoint(sketch, "E128.1", {"position": v(-243.54, 0) * mm});
            skPoint(sketch, "E129.0", {"position": v(-73.54, 0) * mm});
            skPoint(sketch, "E129.1", {"position": v(-61.54, 0) * mm});
            skCircle(sketch, "E130", {"center": v(-237.54, -7.37) * mm, "radius": 9.5 * mm});
            skCircle(sketch, "E131", {"center": v(-67.54, -7.37) * mm, "radius": 9.5 * mm});
            skSolve(sketch);
        }
        {
            var Q0;
            Q0=makeQuery(id+"F31.opExtrude","CAP_FACE",FACE,{"disambiguationData":[OSD([sQuery(id+"F30.wireOp",EDGE,"E114.bottom"),sQuery(id+"F30.wireOp",EDGE,"E114.top"),sQuery(id+"F30.wireOp",EDGE,"E114.left"),sQuery(id+"F30.wireOp",EDGE,"E114.right"),sQuery(id+"F30.wireOp",EDGE,"E115.bottom"),sQuery(id+"F30.wireOp",EDGE,"E115.top"),sQuery(id+"F30.wireOp",EDGE,"E115.left"),sQuery(id+"F30.wireOp",EDGE,"E115.right"),sQuery(id+"F30.wireOp",EDGE,"E118.MirrorCS"),sQuery(id+"F30.wireOp",EDGE,"E119.MirrorCS"),sQuery(id+"F30.wireOp",EDGE,"E120.MirrorCS"),sQuery(id+"F30.wireOp",EDGE,"E121.MirrorCS"),sQuery(id+"F30.wireOp",EDGE,"E122.bottom"),sQuery(id+"F30.wireOp",EDGE,"E122.top"),sQuery(id+"F30.wireOp",EDGE,"E122.left"),sQuery(id+"F30.wireOp",EDGE,"E122.right")])],"isStart":false});
            var sketch = newSketch(context, id + "F34", { "sketchPlane" : qUnion([Q0])});
            skLineSegment(sketch, "E132.bottom", {"start": v(-52.54, -184.5) * mm, "end": v(-252.54, -184.5) * mm});
            skLineSegment(sketch, "E132.top", {"start": v(-52.54, 15.5) * mm, "end": v(-252.54, 15.5) * mm});
            skLineSegment(sketch, "E132.left", {"start": v(-52.54, -184.5) * mm, "end": v(-52.54, 15.5) * mm});
            skLineSegment(sketch, "E132.right", {"start": v(-252.54, -184.5) * mm, "end": v(-252.54, 15.5) * mm});
            skPoint(sketch, "E132.middle", {"position": v(-152.54, -84.5) * mm});
            skPoint(sketch, "E133", {"position": v(-262.54, -84.5) * mm});
            skPoint(sketch, "E134", {"position": v(-152.54, 25.5) * mm});
            skSolve(sketch);
        }
        {
            var Q0;
            Q0=makeQuery(id+"F34.imprint","IMPRINT",FACE,{"disambiguationData":[TD([[makeQuery(id+"F34.imprint","IMPRINT",EDGE,{"derivedFrom":sQuery(id+"F34.wireOp",EDGE,"E132.bottom")}),-1.0]])]});
            extrude(context, id + "F35", {"entities" : qUnion([Q0]), "operationType" : NewBodyOperationType.ADD, "depth" : 10 * mm});
        }
    });
